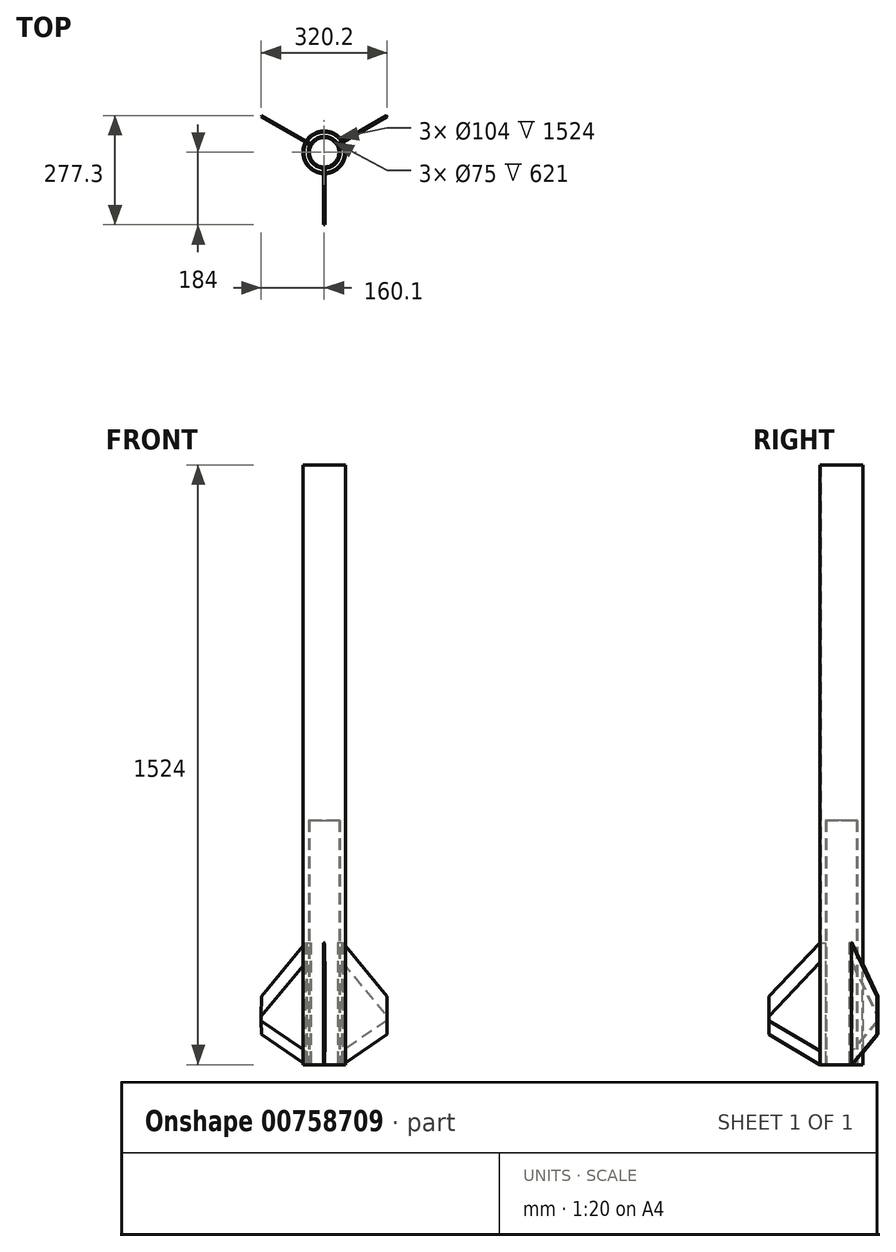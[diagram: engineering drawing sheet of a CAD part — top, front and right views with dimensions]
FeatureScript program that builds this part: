
annotation { "Feature Type Name" : "Feature", "Feature Type Description" : "" }
export const myFeature = defineFeature(function(context is Context, id is Id, definition is map)
    precondition{}
    {
        {
            var Q0;
            Q0=qCreatedBy(makeId("Top.planeOp"),FACE);
            var sketch = newSketch(context, id + "F0", { "sketchPlane" : qUnion([Q0])});
            skCircle(sketch, "E0", {"center": v(0, 0) * mm, "radius": 54 * mm});
            skCircle(sketch, "E1", {"center": v(0, 0) * mm, "radius": 52 * mm});
            skSolve(sketch);
        }
        {
            var Q0;
            Q0=makeQuery(id+"F0.imprint","IMPRINT",FACE,{"disambiguationData":[TD([[makeQuery(id+"F0.imprint","IMPRINT",EDGE,{"derivedFrom":sQuery(id+"F0.wireOp",EDGE,"E0")}),1.0]])]});
            extrude(context, id + "F1", {"entities" : qUnion([Q0]), "depth" : 1524 * mm, "offsetDistance" : 25 * mm});
        }
        {
            var Q0;
            Q0=qCreatedBy(makeId("Front.planeOp"),FACE);
            var sketch = newSketch(context, id + "F2", { "sketchPlane" : qUnion([Q0])});
            skLineSegment(sketch, "E2", {"start": v(0, 0) * mm, "end": v(1.5, 0) * mm});
            skLineSegment(sketch, "E3", {"start": v(1.5, 0) * mm, "end": v(-1.5, 0) * mm});
            skLineSegment(sketch, "E4", {"start": v(-1.5, 0) * mm, "end": v(-1.5, 310) * mm});
            skLineSegment(sketch, "E5", {"start": v(1.5, 0) * mm, "end": v(1.5, 310) * mm});
            skLineSegment(sketch, "E6", {"start": v(1.5, 310) * mm, "end": v(-1.5, 310) * mm});
            skSolve(sketch);
        }
        {
            var Q0;
            Q0 = qSketchRegion(id + "F2", true);
            extrude(context, id + "F3", {"entities" : qUnion([Q0]), "operationType" : NewBodyOperationType.ADD, "depth" : 184 * mm, "offsetDistance" : 25 * mm});
        }
        {
            var Q0;
            {var subQ1=sQuery(id+"F0.wireOp",EDGE,"E0");var subQ3=sQuery(id+"F2.wireOp",EDGE,"E4");Q0=makeQuery(id+"F3.boolean.opBoolean","SPLIT",FACE,{"disambiguationData":[TD([makeQuery(id+"F1.opExtrude","SWEPT_FACE",FACE,{"disambiguationData":[OSD([subQ1])]})])],"derivedFrom":makeQuery(id+"F3.opExtrude","SWEPT_FACE",FACE,{"disambiguationData":[OSD([subQ3])]})});}
            var sketch = newSketch(context, id + "F4", { "sketchPlane" : qUnion([Q0])});
            skLineSegment(sketch, "E7", {"start": v(53.98, 0) * mm, "end": v(184, 76.77) * mm});
            skLineSegment(sketch, "E8", {"start": v(184, 76.77) * mm, "end": v(184, 173.77) * mm});
            skLineSegment(sketch, "E9", {"start": v(184, 173.77) * mm, "end": v(53.98, 310) * mm});
            skSolve(sketch);
        }
        {
            var Q0;
            {var subQ0=sQuery(id+"F4.wireOp",EDGE,"E9");Q0=makeQuery(id+"F4.imprint","IMPRINT",FACE,{"disambiguationData":[TD([[makeQuery(id+"F4.imprint","IMPRINT",EDGE,{"derivedFrom":subQ0}),-1.0]])]});}
            var Q1;
            {var subQ0=sQuery(id+"F4.wireOp",EDGE,"E7");Q1=makeQuery(id+"F4.imprint","IMPRINT",FACE,{"disambiguationData":[TD([[makeQuery(id+"F4.imprint","IMPRINT",EDGE,{"derivedFrom":subQ0}),-1.0]])]});}
            extrude(context, id + "F5", {"entities" : qUnion([Q0, Q1]), "operationType" : NewBodyOperationType.REMOVE, "oppositeDirection" : true, "depth" : 25 * mm, "offsetDistance" : 25 * mm});
        }
        {
            var Q0;
            Q0=qCreatedBy(makeId("Top.planeOp"),FACE);
            var sketch = newSketch(context, id + "F6", { "sketchPlane" : qUnion([Q0])});
            skCircle(sketch, "E10", {"center": v(0, 0) * mm, "radius": 34.76 * mm});
            skSolve(sketch);
        }
        {
            var Q0;
            Q0 = qSketchRegion(id + "F6", true);
            extrude(context, id + "F7", {"entities" : qUnion([Q0]), "operationType" : NewBodyOperationType.REMOVE, "depth" : 269 * mm, "offsetDistance" : 25 * mm});
        }
        {
            var Q0;
            {var subQ1=sQuery(id+"F0.wireOp",EDGE,"E0");var subQ3=sQuery(id+"F2.wireOp",EDGE,"E5");Q0=makeQuery(id+"F5.boolean.opBoolean","INTERSECT",EDGE,{"derivedFrom":[makeQuery(id+"F3.boolean.opBoolean","SPLIT",FACE,{"disambiguationData":[TD([makeQuery(id+"F1.opExtrude","SWEPT_FACE",FACE,{"disambiguationData":[OSD([subQ1])]})])],"derivedFrom":makeQuery(id+"F3.opExtrude","SWEPT_FACE",FACE,{"disambiguationData":[OSD([subQ3])]})}),makeQuery(id+"F5.opExtrude","SWEPT_FACE",FACE,{"disambiguationData":[OSD([sQuery(id+"F4.wireOp",EDGE,"E9")])]})]});}
            var Q1;
            Q1=makeQuery(id+"F5.boolean.opBoolean","COPY",EDGE,{"derivedFrom":makeQuery(id+"F5.opExtrude","CAP_EDGE",EDGE,{"disambiguationData":[OSD([sQuery(id+"F4.wireOp",EDGE,"E9")])],"isStart":true})});
            chamfer(context, id + "F8", {"entities" : qUnion([Q0, Q1]), "chamferType" : ChamferType.OFFSET_ANGLE, "width" : 35 * mm, "oppositeDirection" : true, "angle" : 2.4 * degree, "tangentPropagation" : true});
        }
        {
            var Q0;
            {var subQ1=sQuery(id+"F0.wireOp",EDGE,"E0");var subQ3=sQuery(id+"F2.wireOp",EDGE,"E5");Q0=makeQuery(id+"F5.boolean.opBoolean","INTERSECT",EDGE,{"derivedFrom":[makeQuery(id+"F3.boolean.opBoolean","SPLIT",FACE,{"disambiguationData":[TD([makeQuery(id+"F1.opExtrude","SWEPT_FACE",FACE,{"disambiguationData":[OSD([subQ1])]})])],"derivedFrom":makeQuery(id+"F3.opExtrude","SWEPT_FACE",FACE,{"disambiguationData":[OSD([subQ3])]})}),makeQuery(id+"F5.opExtrude","SWEPT_FACE",FACE,{"disambiguationData":[OSD([sQuery(id+"F4.wireOp",EDGE,"E7")])]})]});}
            var Q1;
            Q1=makeQuery(id+"F5.boolean.opBoolean","COPY",EDGE,{"derivedFrom":makeQuery(id+"F5.opExtrude","CAP_EDGE",EDGE,{"disambiguationData":[OSD([sQuery(id+"F4.wireOp",EDGE,"E7")])],"isStart":true})});
            chamfer(context, id + "F9", {"entities" : qUnion([Q0, Q1]), "chamferType" : ChamferType.OFFSET_ANGLE, "width" : 30 * mm, "oppositeDirection" : true, "angle" : 2.4 * degree, "tangentPropagation" : true});
        }
        {
            var Q0;
            Q0=makeQuery(id+"F3.boolean.opBoolean","MERGE",FACE,{"derivedFrom":[makeQuery(id+"F1.opExtrude","CAP_FACE",FACE,{"disambiguationData":[OSD([sQuery(id+"F0.wireOp",EDGE,"E0"),sQuery(id+"F0.wireOp",EDGE,"E1")])],"isStart":true}),makeQuery(id+"F3.opExtrude","SWEPT_FACE",FACE,{"disambiguationData":[OSD([sQuery(id+"F2.wireOp",EDGE,"E3")])]})]});
            var sketch = newSketch(context, id + "F10", { "sketchPlane" : qUnion([Q0])});
            skLineSegment(sketch, "E11.bottom", {"start": v(-1.5, 0) * mm, "end": v(1.5, 0) * mm});
            skLineSegment(sketch, "E11.top", {"start": v(-1.5, 34.76) * mm, "end": v(1.5, 34.76) * mm});
            skLineSegment(sketch, "E11.left", {"start": v(-1.5, 0) * mm, "end": v(-1.5, 34.76) * mm});
            skLineSegment(sketch, "E11.right", {"start": v(1.5, 0) * mm, "end": v(1.5, 34.76) * mm});
            skSolve(sketch);
        }
        {
            var Q0;
            Q0=makeQuery(id+"F10.imprint","IMPRINT",FACE,{"disambiguationData":[TD([[makeQuery(id+"F10.imprint","IMPRINT",EDGE,{"derivedFrom":sQuery(id+"F10.wireOp",EDGE,"E11.bottom")}),-1.0]])]});
            extrude(context, id + "F11", {"entities" : qUnion([Q0]), "operationType" : NewBodyOperationType.REMOVE, "oppositeDirection" : true, "depth" : 700 * mm, "offsetDistance" : 25 * mm});
        }
        {
            var Q0;
            Q0=qCreatedBy(makeId("Top.planeOp"),FACE);
            var sketch = newSketch(context, id + "F12", { "sketchPlane" : qUnion([Q0])});
            skCircle(sketch, "E12", {"center": v(0, 0) * mm, "radius": 37.5 * mm});
            skCircle(sketch, "E13", {"center": v(0, 0) * mm, "radius": 40.19 * mm});
            skSolve(sketch);
        }
        {
            var Q0;
            Q0=makeQuery(id+"F12.imprint","IMPRINT",FACE,{"disambiguationData":[TD([[makeQuery(id+"F12.imprint","IMPRINT",EDGE,{"derivedFrom":sQuery(id+"F12.wireOp",EDGE,"E12")}),1.0]])]});
            var Q1;
            Q1=makeQuery(id+"F12.imprint","IMPRINT",FACE,{"disambiguationData":[TD([[makeQuery(id+"F12.imprint","IMPRINT",EDGE,{"derivedFrom":sQuery(id+"F12.wireOp",EDGE,"E12")}),-1.0]])]});
            extrude(context, id + "F13", {"entities" : qUnion([Q0, Q1]), "operationType" : NewBodyOperationType.REMOVE, "depth" : 670 * mm, "offsetDistance" : 25 * mm});
        }
        {
            var Q0;
            Q0=qCreatedBy(makeId("Top.planeOp"),FACE);
            var sketch = newSketch(context, id + "F14", { "sketchPlane" : qUnion([Q0])});
            skCircle(sketch, "E14", {"center": v(0, 0) * mm, "radius": 37.5 * mm});
            skCircle(sketch, "E15", {"center": v(0, 0) * mm, "radius": 40.2 * mm});
            skSolve(sketch);
        }
        {
            var Q0;
            Q0=makeQuery(id+"F14.imprint","IMPRINT",FACE,{"disambiguationData":[TD([[makeQuery(id+"F14.imprint","IMPRINT",EDGE,{"derivedFrom":sQuery(id+"F14.wireOp",EDGE,"E14")}),-1.0]])]});
            extrude(context, id + "F15", {"entities" : qUnion([Q0]), "operationType" : NewBodyOperationType.ADD, "depth" : 621 * mm, "offsetDistance" : 25 * mm});
        }
        {
            var Q0;
            Q0=makeQuery(id+"F1.opExtrude","SWEPT_BODY",BODY,{"disambiguationData":[OSD([sQuery(id+"F0.wireOp",EDGE,"E0"),sQuery(id+"F0.wireOp",EDGE,"E1")])]});
            var Q1;
            Q1=makeQuery(id+"F1.opExtrude","CAP_EDGE",EDGE,{"disambiguationData":[OSD([sQuery(id+"F0.wireOp",EDGE,"E1")])],"isStart":false});
            circularPattern(context, id + "F16", {"entities" : qUnion([Q0]), "axis" : qUnion([Q1]), "angle" : 360 * degree, "instanceCount" : 3, "equalSpace" : true});
        }
    });
